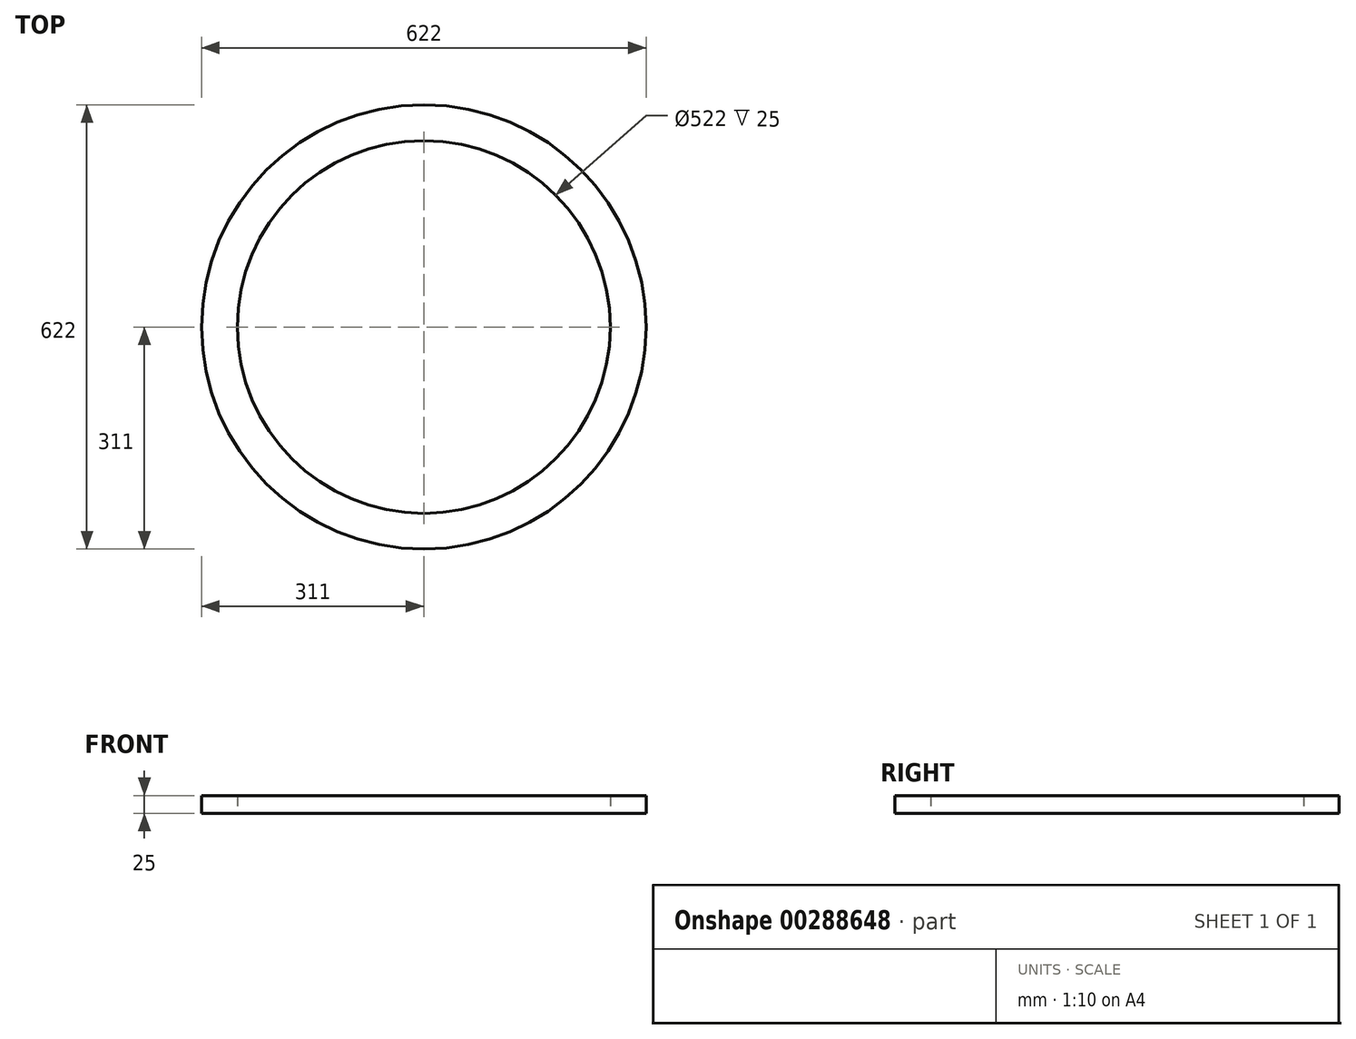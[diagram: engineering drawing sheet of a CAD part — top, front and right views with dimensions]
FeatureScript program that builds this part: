
annotation { "Feature Type Name" : "Feature", "Feature Type Description" : "" }
export const myFeature = defineFeature(function(context is Context, id is Id, definition is map)
    precondition{}
    {
        {
            var Q0;
            Q0=qCreatedBy(makeId("Top.planeOp"),FACE);
            var sketch = newSketch(context, id + "F0", { "sketchPlane" : qUnion([Q0])});
            skCircle(sketch, "E0", {"center": v(0, 0) * mm, "radius": 311 * mm});
            skCircle(sketch, "E1", {"center": v(0, 0) * mm, "radius": 261 * mm});
            skSolve(sketch);
        }
        {
            var Q0;
            Q0=makeQuery(id+"F0.imprint","IMPRINT",FACE,{"disambiguationData":[TD([[makeQuery(id+"F0.imprint","IMPRINT",EDGE,{"derivedFrom":sQuery(id+"F0.wireOp",EDGE,"E0")}),1.0]])]});
            extrude(context, id + "F1", {"entities" : qUnion([Q0]), "depth" : 25 * mm});
        }
    });
